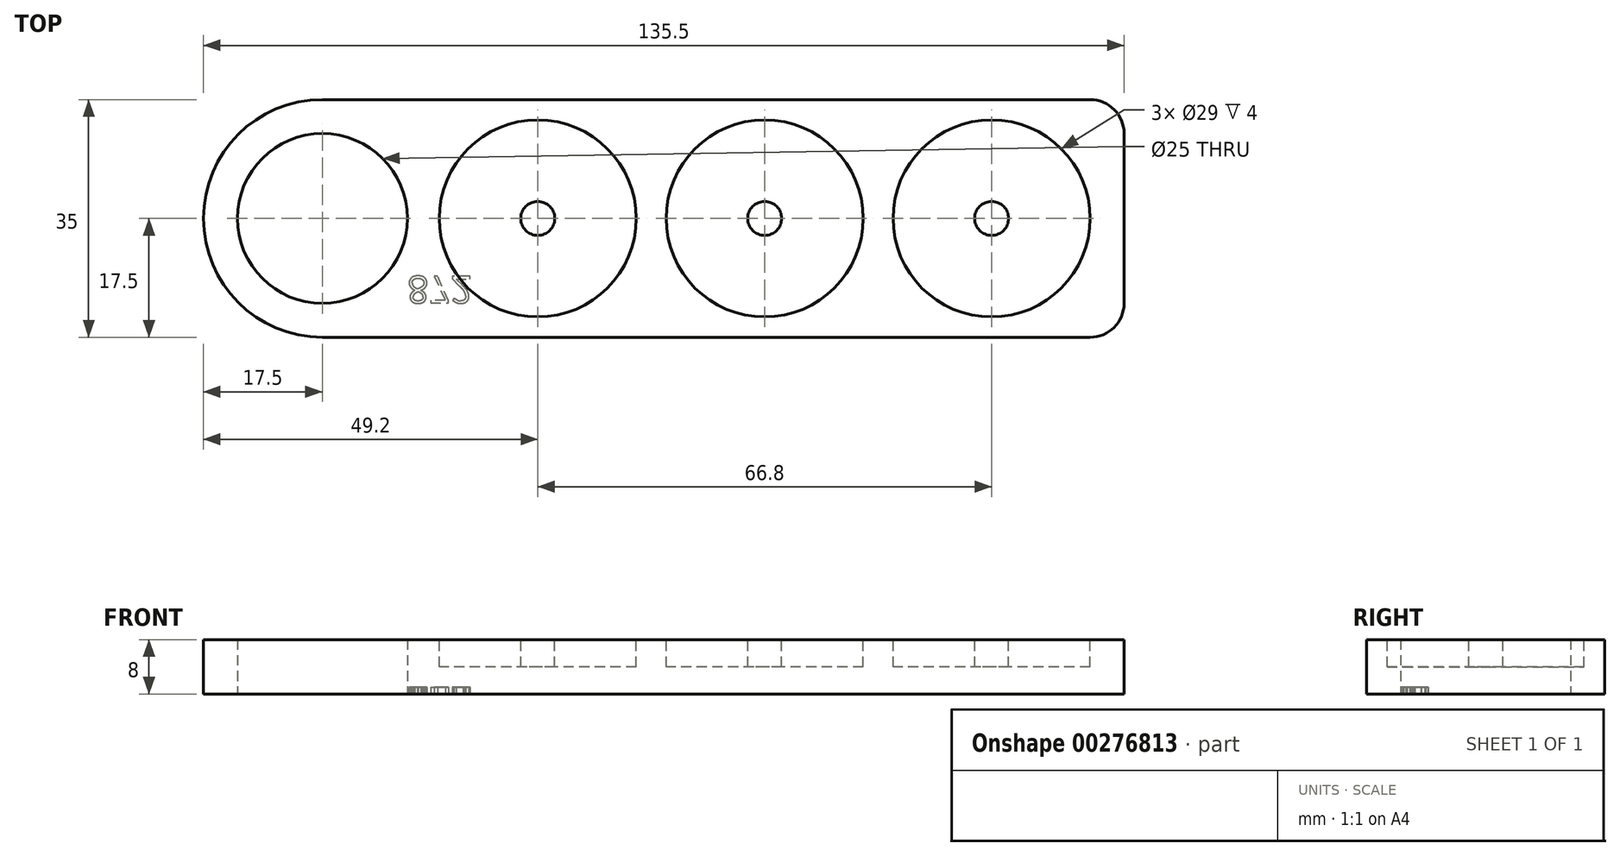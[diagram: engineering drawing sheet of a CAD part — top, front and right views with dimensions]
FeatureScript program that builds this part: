
annotation { "Feature Type Name" : "Feature", "Feature Type Description" : "" }
export const myFeature = defineFeature(function(context is Context, id is Id, definition is map)
    precondition{}
    {
        {
            var Q0;
            Q0=qCreatedBy(makeId("Top.planeOp"),FACE);
            var sketch = newSketch(context, id + "F0", { "sketchPlane" : qUnion([Q0])});
            skLineSegment(sketch, "E0.bottom", {"start": v(17.5, 0) * mm, "end": v(130.5, 0) * mm});
            skLineSegment(sketch, "E0.top", {"start": v(17.5, 35) * mm, "end": v(130.5, 35) * mm});
            skLineSegment(sketch, "E0.left", {"start": v(0, 17.5) * mm, "end": v(0, 17.5) * mm});
            skLineSegment(sketch, "E0.right", {"start": v(135.5, 5) * mm, "end": v(135.5, 30) * mm});
            skLineSegment(sketch, "E1.bottom", {"start": v(0, 0) * mm, "end": v(17.5, 0) * mm, "construction": true});
            skLineSegment(sketch, "E1.top", {"start": v(0, 17.5) * mm, "end": v(17.5, 17.5) * mm, "construction": true});
            skLineSegment(sketch, "E1.left", {"start": v(0, 0) * mm, "end": v(0, 17.5) * mm, "construction": true});
            skLineSegment(sketch, "E1.right", {"start": v(17.5, 0) * mm, "end": v(17.5, 17.5) * mm, "construction": true});
            skCircle(sketch, "E2", {"center": v(17.5, 17.5) * mm, "radius": 12.5 * mm});
            skPoint(sketch, "E3.visualSharp", {"position": v(0, 0) * mm});
            skArc(sketch, "E3.filletArc", {"start": v(0, 17.5) * mm, "mid": v(5.13, 5.13) * mm, "end": v(17.5, 0) * mm});
            skPoint(sketch, "E4.visualSharp", {"position": v(0, 35) * mm});
            skArc(sketch, "E4.filletArc", {"start": v(17.5, 35) * mm, "mid": v(5.13, 29.87) * mm, "end": v(0, 17.5) * mm});
            skPoint(sketch, "E5.visualSharp", {"position": v(135.5, 35) * mm});
            skArc(sketch, "E5.filletArc", {"start": v(135.5, 30) * mm, "mid": v(134.04, 33.54) * mm, "end": v(130.5, 35) * mm});
            skPoint(sketch, "E6.visualSharp", {"position": v(135.5, 0) * mm});
            skArc(sketch, "E6.filletArc", {"start": v(130.5, 0) * mm, "mid": v(134.04, 1.46) * mm, "end": v(135.5, 5) * mm});
            skSolve(sketch);
        }
        {
            var Q0;
            Q0=makeQuery(id+"F0.imprint","IMPRINT",FACE,{"disambiguationData":[TD([[makeQuery(id+"F0.imprint","IMPRINT",EDGE,{"derivedFrom":sQuery(id+"F0.wireOp",EDGE,"E0.bottom")}),1.0]])]});
            extrude(context, id + "F1", {"entities" : qUnion([Q0]), "depth" : 8 * mm});
        }
        {
            var Q0;
            Q0=makeQuery(id+"F1.opExtrude","CAP_FACE",FACE,{"disambiguationData":[OSD([sQuery(id+"F0.wireOp",EDGE,"E0.bottom"),sQuery(id+"F0.wireOp",EDGE,"E0.top"),sQuery(id+"F0.wireOp",EDGE,"E0.right"),sQuery(id+"F0.wireOp",EDGE,"E2"),sQuery(id+"F0.wireOp",EDGE,"E3.filletArc"),sQuery(id+"F0.wireOp",EDGE,"E4.filletArc"),sQuery(id+"F0.wireOp",EDGE,"E5.filletArc"),sQuery(id+"F0.wireOp",EDGE,"E6.filletArc")])],"isStart":false});
            var sketch = newSketch(context, id + "F2", { "sketchPlane" : qUnion([Q0])});
            skLineSegment(sketch, "E7.bottom", {"start": v(0, 0) * mm, "end": v(49.2, 0) * mm, "construction": true});
            skLineSegment(sketch, "E7.top", {"start": v(0, 17.5) * mm, "end": v(49.2, 17.5) * mm, "construction": true});
            skLineSegment(sketch, "E7.left", {"start": v(0, 0) * mm, "end": v(0, 17.5) * mm, "construction": true});
            skLineSegment(sketch, "E7.right", {"start": v(49.2, 0) * mm, "end": v(49.2, 17.5) * mm, "construction": true});
            skLineSegment(sketch, "E8", {"start": v(49.2, 17.5) * mm, "end": v(82.6, 17.5) * mm, "construction": true});
            skLineSegment(sketch, "E9", {"start": v(82.6, 17.5) * mm, "end": v(116, 17.5) * mm, "construction": true});
            skCircle(sketch, "E10", {"center": v(49.2, 17.5) * mm, "radius": 14.5 * mm});
            skCircle(sketch, "E11", {"center": v(82.6, 17.5) * mm, "radius": 14.5 * mm});
            skCircle(sketch, "E12", {"center": v(116, 17.5) * mm, "radius": 14.5 * mm});
            skCircle(sketch, "E13", {"center": v(116, 17.5) * mm, "radius": 2.5 * mm});
            skCircle(sketch, "E14", {"center": v(82.6, 17.5) * mm, "radius": 2.5 * mm});
            skCircle(sketch, "E15", {"center": v(49.2, 17.5) * mm, "radius": 2.5 * mm});
            skSolve(sketch);
        }
        {
            var Q0;
            Q0=makeQuery(id+"F2.imprint","IMPRINT",FACE,{"disambiguationData":[TD([[makeQuery(id+"F2.imprint","IMPRINT",EDGE,{"derivedFrom":sQuery(id+"F2.wireOp",EDGE,"E10")}),1.0]])]});
            var Q1;
            Q1=makeQuery(id+"F2.imprint","IMPRINT",FACE,{"disambiguationData":[TD([[makeQuery(id+"F2.imprint","IMPRINT",EDGE,{"derivedFrom":sQuery(id+"F2.wireOp",EDGE,"E11")}),1.0]])]});
            var Q2;
            Q2=makeQuery(id+"F2.imprint","IMPRINT",FACE,{"disambiguationData":[TD([[makeQuery(id+"F2.imprint","IMPRINT",EDGE,{"derivedFrom":sQuery(id+"F2.wireOp",EDGE,"E12")}),1.0]])]});
            extrude(context, id + "F3", {"entities" : qUnion([Q0, Q1, Q2]), "operationType" : NewBodyOperationType.REMOVE, "oppositeDirection" : true, "depth" : 4 * mm});
        }
        {
            var Q0;
            Q0=makeQuery(id+"F1.opExtrude","CAP_FACE",FACE,{"disambiguationData":[OSD([sQuery(id+"F0.wireOp",EDGE,"E0.bottom"),sQuery(id+"F0.wireOp",EDGE,"E0.top"),sQuery(id+"F0.wireOp",EDGE,"E0.right"),sQuery(id+"F0.wireOp",EDGE,"E2"),sQuery(id+"F0.wireOp",EDGE,"E3.filletArc"),sQuery(id+"F0.wireOp",EDGE,"E4.filletArc"),sQuery(id+"F0.wireOp",EDGE,"E5.filletArc"),sQuery(id+"F0.wireOp",EDGE,"E6.filletArc")])],"isStart":true});
            var sketch = newSketch(context, id + "F4", { "sketchPlane" : qUnion([Q0])});
            skLineSegment(sketch, "E16.bottom", {"start": v(0, 0) * mm, "end": v(30, 0) * mm, "construction": true});
            skLineSegment(sketch, "E16.top", {"start": v(0, -5) * mm, "end": v(30, -5) * mm, "construction": true});
            skLineSegment(sketch, "E16.left", {"start": v(0, 0) * mm, "end": v(0, -5) * mm, "construction": true});
            skLineSegment(sketch, "E16.right", {"start": v(30, 0) * mm, "end": v(30, -5) * mm, "construction": true});
            skText(sketch, "E17", { "text": "872", "fontName": "OpenSans-Regular.ttf"});
            const initialGuessF4  = {"E17": [0.03, -0.009, 1, 0, 0.004]};
            skSetInitialGuess(sketch, initialGuessF4);
            skSolve(sketch);
        }
        {
            var Q0;
            Q0 = qSketchRegion(id + "F4", true);
            extrude(context, id + "F5", {"entities" : qUnion([Q0]), "operationType" : NewBodyOperationType.REMOVE, "oppositeDirection" : true, "depth" : 1 * mm});
        }
    });
